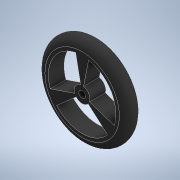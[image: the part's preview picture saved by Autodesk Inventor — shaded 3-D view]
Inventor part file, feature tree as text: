
AUTODESK INVENTOR PART (.ipt)
format: ipt  version: 2022 (Build 260153000, 153)  size: 165,888 bytes
history: native  units: mm
features: extrude x3, sketch x3, fillet x1
ambient origin geometry x8: Origin, YZ Plane, XZ Plane, XY Plane, X Axis, Y Axis, Z Axis, Center Point
bodies: Solid1 (feature_tree)
feature tree (7):
  extrude  "Extrusion1"  Depth=7.0mm
  fillet  "Fillet1"  Radius=7.0mm
  extrude  "Extrusion2"  Depth=3.5mm
  extrude  "Extrusion3"  Depth=7.0mm TaperAngle=0.0deg
  sketch  "Sketch1"  dims[d0=40.0mm d1=30.0mm d2=7.0mm d3=0.0mm]
  sketch  "Sketch2"  dims[d4=3.5mm d5=3.0mm]
  sketch  "Sketch3"  dims[d6=7.0mm d7=7.0mm d8=0.0mm d9=0.0mm d10=30.0mm d11=30.0mm d13=360.0deg d15=7.0mm d16=0.0mm]
